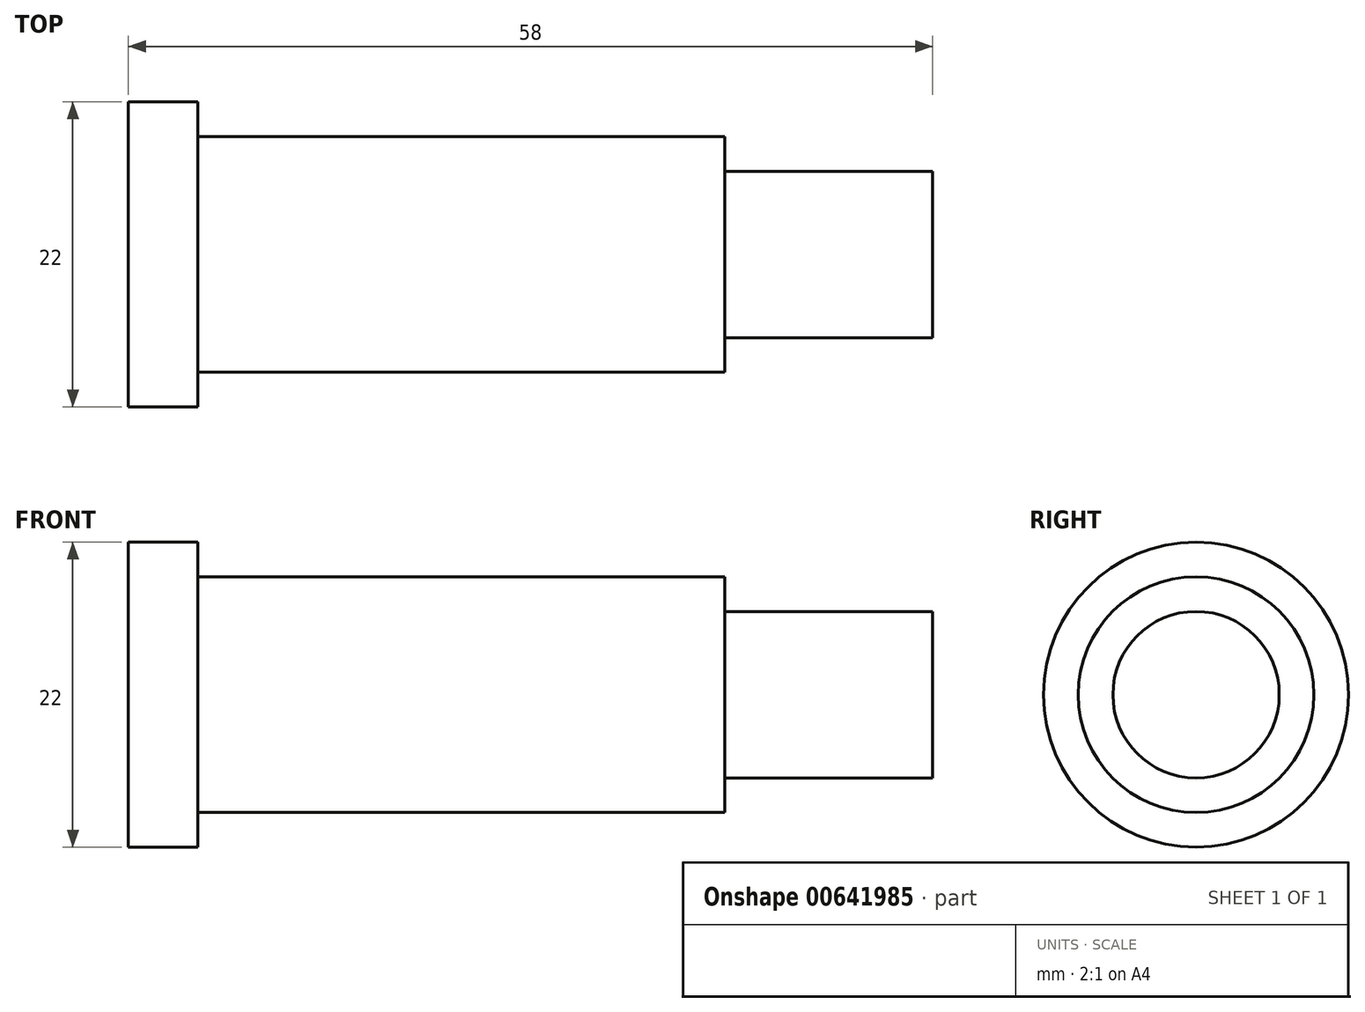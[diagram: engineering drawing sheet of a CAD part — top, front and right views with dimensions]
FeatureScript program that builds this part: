
annotation { "Feature Type Name" : "Feature", "Feature Type Description" : "" }
export const myFeature = defineFeature(function(context is Context, id is Id, definition is map)
    precondition{}
    {
        {
            var Q0;
            Q0=qCreatedBy(makeId("Front.planeOp"),FACE);
            var sketch = newSketch(context, id + "F0", { "sketchPlane" : qUnion([Q0])});
            skLineSegment(sketch, "E0", {"start": v(0, 0) * mm, "end": v(0, 11) * mm});
            skLineSegment(sketch, "E1", {"start": v(0, 11) * mm, "end": v(5, 11) * mm});
            skLineSegment(sketch, "E2", {"start": v(5, 11) * mm, "end": v(5, 8.5) * mm});
            skLineSegment(sketch, "E3", {"start": v(5, 8.5) * mm, "end": v(43, 8.5) * mm});
            skLineSegment(sketch, "E4", {"start": v(43, 8.5) * mm, "end": v(43, 6) * mm});
            skLineSegment(sketch, "E5", {"start": v(43, 6) * mm, "end": v(58, 6) * mm});
            skLineSegment(sketch, "E6", {"start": v(58, 6) * mm, "end": v(58, 0) * mm});
            skLineSegment(sketch, "E7", {"start": v(58, 0) * mm, "end": v(0, 0) * mm});
            skSolve(sketch);
        }
        {
            var Q0;
            Q0=makeQuery(id+"F0.imprint","IMPRINT",FACE,{"disambiguationData":[TD([[makeQuery(id+"F0.imprint","IMPRINT",EDGE,{"derivedFrom":sQuery(id+"F0.wireOp",EDGE,"E0")}),-1.0]])]});
            var Q1;
            Q1=sQuery(id+"F0.wireOp",EDGE,"E7");
            revolve(context, id + "F1", {"entities" : qUnion([Q0]), "axis" : qUnion([Q1]), "revolveType" : RevolveType.FULL});
        }
    });
